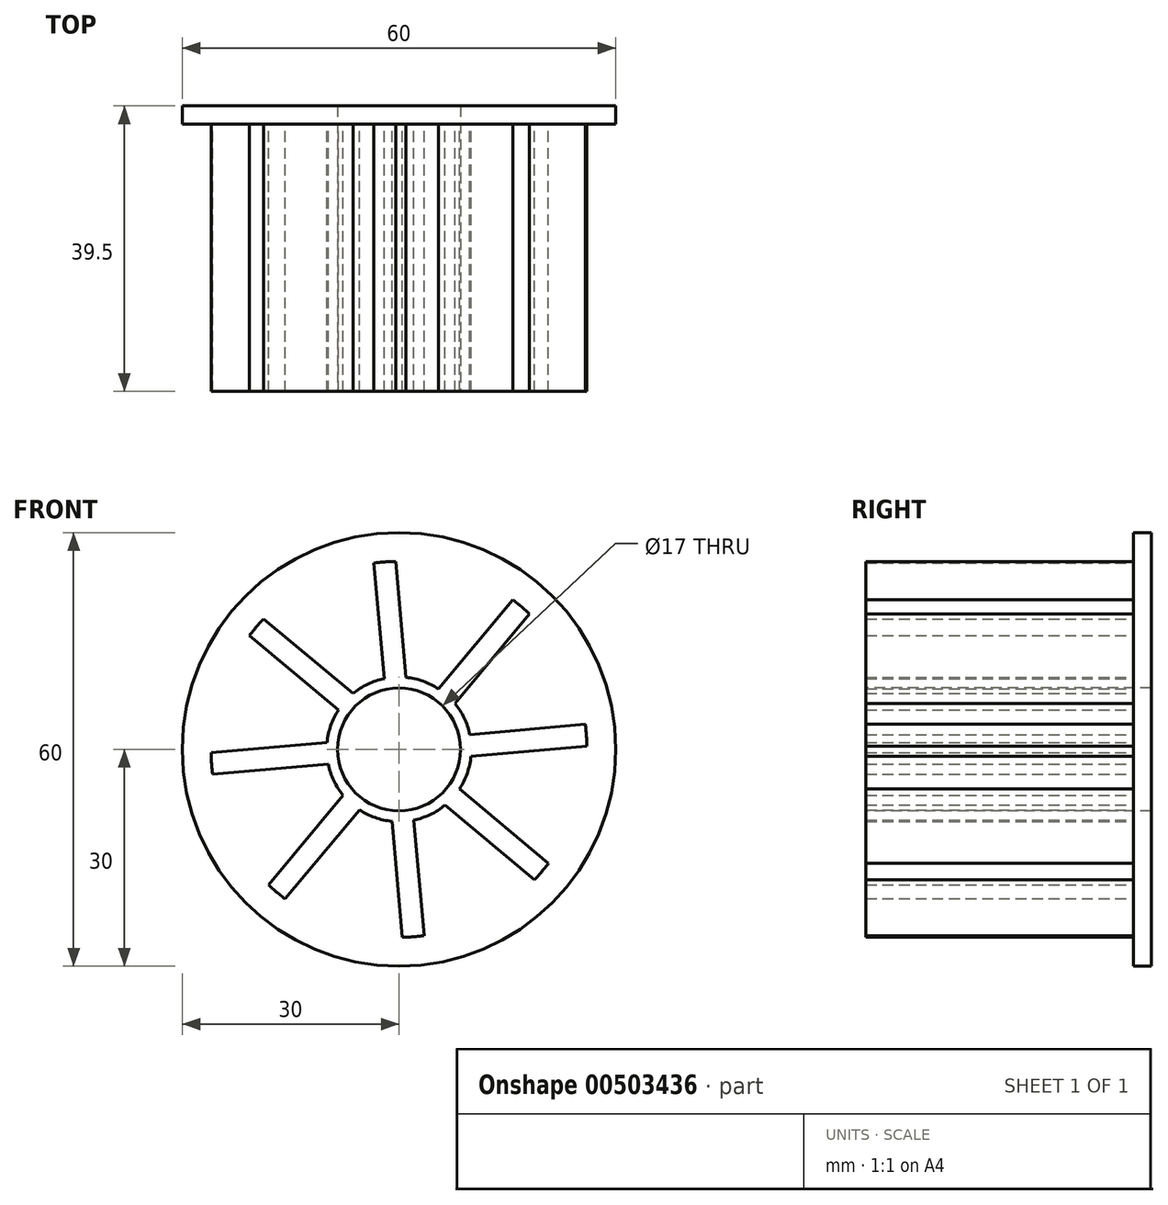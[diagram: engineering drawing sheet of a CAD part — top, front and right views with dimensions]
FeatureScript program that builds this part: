
annotation { "Feature Type Name" : "Feature", "Feature Type Description" : "" }
export const myFeature = defineFeature(function(context is Context, id is Id, definition is map)
    precondition{}
    {
        {
            var Q0;
            Q0=qCreatedBy(makeId("Front.planeOp"),FACE);
            var sketch = newSketch(context, id + "F0", { "sketchPlane" : qUnion([Q0])});
            skCircle(sketch, "E0", {"center": v(0, 0) * mm, "radius": 30 * mm});
            skCircle(sketch, "E1", {"center": v(0, 0) * mm, "radius": 8.5 * mm});
            skSolve(sketch);
        }
        {
            var Q0;
            Q0 = qSketchRegion(id + "F0", true);
            extrude(context, id + "F1", {"entities" : qUnion([Q0]), "oppositeDirection" : true, "depth" : 2.5 * mm});
        }
        {
            var Q0;
            Q0=qCreatedBy(makeId("Front.planeOp"),FACE);
            var sketch = newSketch(context, id + "F2", { "sketchPlane" : qUnion([Q0])});
            skCircle(sketch, "E2", {"center": v(0, 0) * mm, "radius": 10 * mm});
            skArc(sketch, "E3", {"start": v(18.71, -18.05) * mm, "mid": v(19.72, -16.94) * mm, "end": v(20.67, -15.77) * mm});
            skLineSegment(sketch, "E4", {"start": v(18.71, -18.05) * mm, "end": v(6.36, -7.72) * mm});
            skLineSegment(sketch, "E5", {"start": v(20.67, -15.77) * mm, "end": v(8.36, -5.48) * mm});
            skLineSegment(sketch, "E6.1.0", {"start": v(25.77, 3.46) * mm, "end": v(9.8, 2.04) * mm});
            skLineSegment(sketch, "E6.1.1", {"start": v(26, 0.47) * mm, "end": v(9.95, -0.96) * mm});
            skArc(sketch, "E6.1.2", {"start": v(26, 0.47) * mm, "mid": v(25.93, 1.97) * mm, "end": v(25.77, 3.46) * mm});
            skLineSegment(sketch, "E6.2.0", {"start": v(15.77, 20.67) * mm, "end": v(5.48, 8.36) * mm});
            skLineSegment(sketch, "E6.2.1", {"start": v(18.05, 18.71) * mm, "end": v(7.72, 6.36) * mm});
            skArc(sketch, "E6.2.2", {"start": v(18.05, 18.71) * mm, "mid": v(16.94, 19.72) * mm, "end": v(15.77, 20.67) * mm});
            skLineSegment(sketch, "E6.3.0", {"start": v(-3.46, 25.77) * mm, "end": v(-2.04, 9.8) * mm});
            skLineSegment(sketch, "E6.3.1", {"start": v(-0.47, 26) * mm, "end": v(0.96, 9.95) * mm});
            skArc(sketch, "E6.3.2", {"start": v(-0.47, 26) * mm, "mid": v(-1.97, 25.93) * mm, "end": v(-3.46, 25.77) * mm});
            skLineSegment(sketch, "E6.4.0", {"start": v(-20.67, 15.77) * mm, "end": v(-8.36, 5.48) * mm});
            skLineSegment(sketch, "E6.4.1", {"start": v(-18.71, 18.05) * mm, "end": v(-6.36, 7.72) * mm});
            skArc(sketch, "E6.4.2", {"start": v(-18.71, 18.05) * mm, "mid": v(-19.72, 16.94) * mm, "end": v(-20.67, 15.77) * mm});
            skLineSegment(sketch, "E6.5.0", {"start": v(-25.77, -3.46) * mm, "end": v(-9.8, -2.04) * mm});
            skLineSegment(sketch, "E6.5.1", {"start": v(-26, -0.47) * mm, "end": v(-9.95, 0.96) * mm});
            skArc(sketch, "E6.5.2", {"start": v(-26, -0.47) * mm, "mid": v(-25.93, -1.97) * mm, "end": v(-25.77, -3.46) * mm});
            skLineSegment(sketch, "E6.6.0", {"start": v(-15.77, -20.67) * mm, "end": v(-5.48, -8.36) * mm});
            skLineSegment(sketch, "E6.6.1", {"start": v(-18.05, -18.71) * mm, "end": v(-7.72, -6.36) * mm});
            skArc(sketch, "E6.6.2", {"start": v(-18.05, -18.71) * mm, "mid": v(-16.94, -19.72) * mm, "end": v(-15.77, -20.67) * mm});
            skLineSegment(sketch, "E6.7.0", {"start": v(3.46, -25.77) * mm, "end": v(2.04, -9.8) * mm});
            skLineSegment(sketch, "E6.7.1", {"start": v(0.47, -26) * mm, "end": v(-0.96, -9.95) * mm});
            skArc(sketch, "E6.7.2", {"start": v(0.47, -26) * mm, "mid": v(1.97, -25.93) * mm, "end": v(3.46, -25.77) * mm});
            skSolve(sketch);
        }
        {
            var Q0;
            {var subQ0=sQuery(id+"F2.wireOp",EDGE,"E2");var subQ8=makeQuery(id+"F2.imprint","INTERSECT",VERTEX,{"derivedFrom":[subQ0,sQuery(id+"F2.wireOp",EDGE,"E6.1.0")]});Q0=makeQuery(id+"F2.imprint","IMPRINT",FACE,{"disambiguationData":[TD([[makeQuery(id+"F2.imprint","IMPRINT",EDGE,{"disambiguationData":[TD([[subQ8,-1.0]])],"derivedFrom":subQ0}),1.0]])]});}
            var Q1;
            {var subQ0=sQuery(id+"F2.wireOp",EDGE,"E6.4.0");Q1=makeQuery(id+"F2.imprint","IMPRINT",FACE,{"disambiguationData":[TD([[makeQuery(id+"F2.imprint","IMPRINT",EDGE,{"derivedFrom":subQ0}),1.0]])]});}
            var Q2;
            {var subQ0=sQuery(id+"F2.wireOp",EDGE,"E6.6.0");Q2=makeQuery(id+"F2.imprint","IMPRINT",FACE,{"disambiguationData":[TD([[makeQuery(id+"F2.imprint","IMPRINT",EDGE,{"derivedFrom":subQ0}),1.0]])]});}
            var Q3;
            {var subQ0=sQuery(id+"F2.wireOp",EDGE,"E6.7.0");Q3=makeQuery(id+"F2.imprint","IMPRINT",FACE,{"disambiguationData":[TD([[makeQuery(id+"F2.imprint","IMPRINT",EDGE,{"derivedFrom":subQ0}),1.0]])]});}
            var Q4;
            Q4=makeQuery(id+"F2.imprint","IMPRINT",FACE,{"disambiguationData":[TD([[makeQuery(id+"F2.imprint","IMPRINT",EDGE,{"derivedFrom":sQuery(id+"F2.wireOp",EDGE,"E3")}),1.0]])]});
            var Q5;
            {var subQ0=sQuery(id+"F2.wireOp",EDGE,"E6.1.0");Q5=makeQuery(id+"F2.imprint","IMPRINT",FACE,{"disambiguationData":[TD([[makeQuery(id+"F2.imprint","IMPRINT",EDGE,{"derivedFrom":subQ0}),1.0]])]});}
            var Q6;
            {var subQ0=sQuery(id+"F2.wireOp",EDGE,"E6.2.0");Q6=makeQuery(id+"F2.imprint","IMPRINT",FACE,{"disambiguationData":[TD([[makeQuery(id+"F2.imprint","IMPRINT",EDGE,{"derivedFrom":subQ0}),1.0]])]});}
            var Q7;
            {var subQ0=sQuery(id+"F2.wireOp",EDGE,"E6.3.0");Q7=makeQuery(id+"F2.imprint","IMPRINT",FACE,{"disambiguationData":[TD([[makeQuery(id+"F2.imprint","IMPRINT",EDGE,{"derivedFrom":subQ0}),1.0]])]});}
            var Q8;
            {var subQ0=sQuery(id+"F2.wireOp",EDGE,"E6.5.0");Q8=makeQuery(id+"F2.imprint","IMPRINT",FACE,{"disambiguationData":[TD([[makeQuery(id+"F2.imprint","IMPRINT",EDGE,{"derivedFrom":subQ0}),1.0]])]});}
            extrude(context, id + "F3", {"entities" : qUnion([Q0, Q1, Q2, Q3, Q4, Q5, Q6, Q7, Q8]), "operationType" : NewBodyOperationType.ADD, "depth" : 37 * mm});
        }
        {
            var Q0;
            Q0=makeQuery(id+"F3.opExtrude","CAP_FACE",FACE,{"disambiguationData":[OSD([sQuery(id+"F2.wireOp",EDGE,"E2"),sQuery(id+"F2.wireOp",EDGE,"E3"),sQuery(id+"F2.wireOp",EDGE,"E4"),sQuery(id+"F2.wireOp",EDGE,"E5"),sQuery(id+"F2.wireOp",EDGE,"E6.1.0"),sQuery(id+"F2.wireOp",EDGE,"E6.1.1"),sQuery(id+"F2.wireOp",EDGE,"E6.1.2"),sQuery(id+"F2.wireOp",EDGE,"E6.2.0"),sQuery(id+"F2.wireOp",EDGE,"E6.2.1"),sQuery(id+"F2.wireOp",EDGE,"E6.2.2"),sQuery(id+"F2.wireOp",EDGE,"E6.3.0"),sQuery(id+"F2.wireOp",EDGE,"E6.3.1"),sQuery(id+"F2.wireOp",EDGE,"E6.3.2"),sQuery(id+"F2.wireOp",EDGE,"E6.4.0"),sQuery(id+"F2.wireOp",EDGE,"E6.4.1"),sQuery(id+"F2.wireOp",EDGE,"E6.4.2"),sQuery(id+"F2.wireOp",EDGE,"E6.5.0"),sQuery(id+"F2.wireOp",EDGE,"E6.5.1"),sQuery(id+"F2.wireOp",EDGE,"E6.5.2"),sQuery(id+"F2.wireOp",EDGE,"E6.6.0"),sQuery(id+"F2.wireOp",EDGE,"E6.6.1"),sQuery(id+"F2.wireOp",EDGE,"E6.6.2"),sQuery(id+"F2.wireOp",EDGE,"E6.7.0"),sQuery(id+"F2.wireOp",EDGE,"E6.7.1"),sQuery(id+"F2.wireOp",EDGE,"E6.7.2")])],"isStart":true});
            extrude(context, id + "F4", {"entities" : qUnion([Q0]), "operationType" : NewBodyOperationType.REMOVE, "oppositeDirection" : true, "depth" : 40 * mm});
        }
    });
